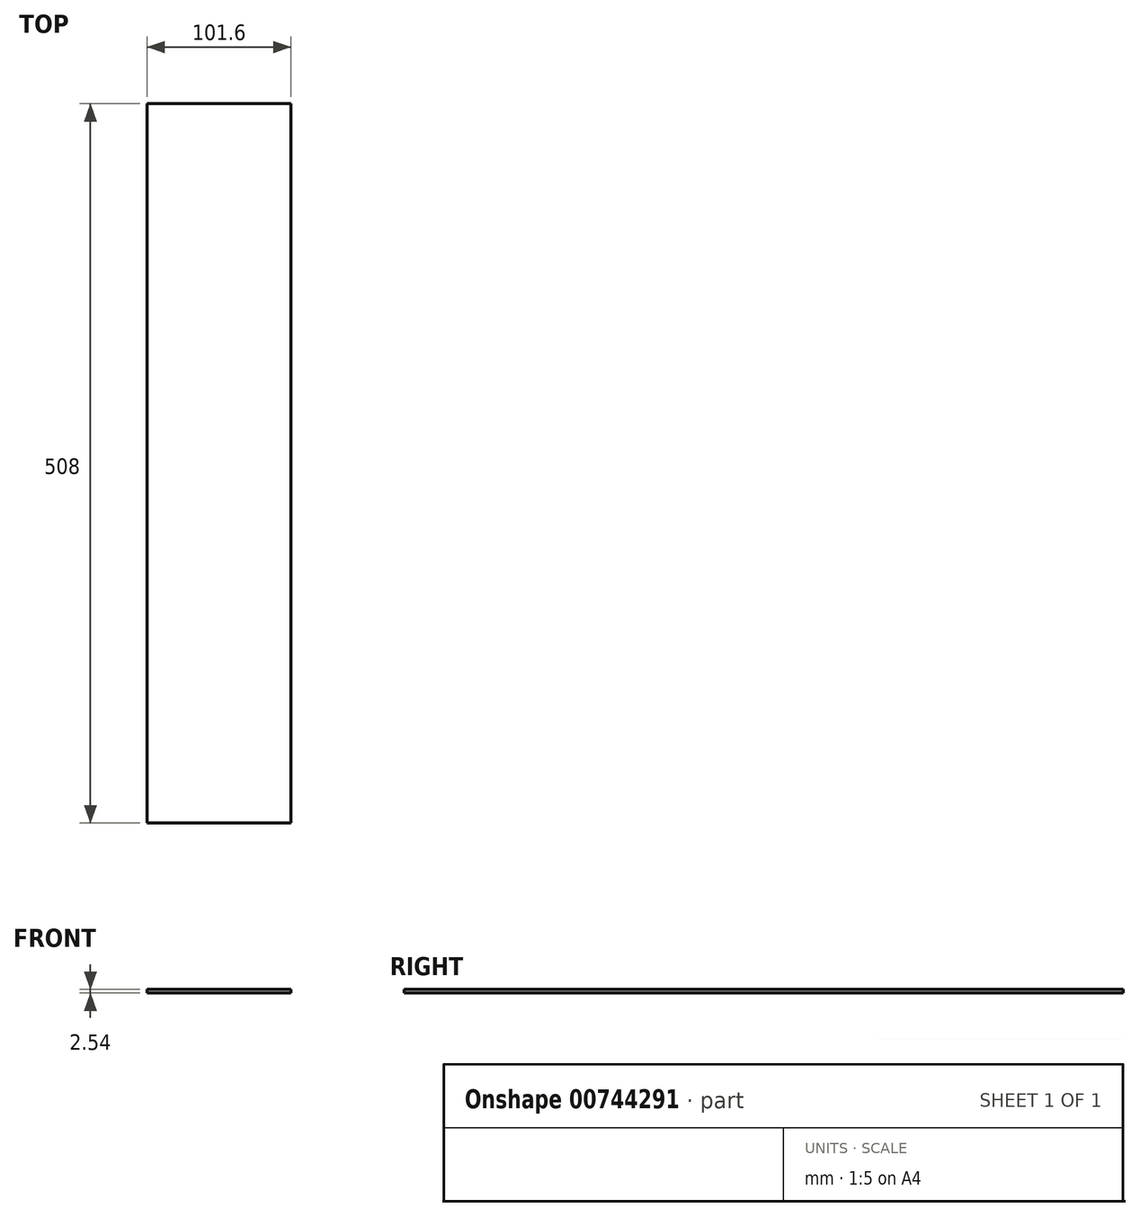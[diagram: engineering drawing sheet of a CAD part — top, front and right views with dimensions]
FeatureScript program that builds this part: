
annotation { "Feature Type Name" : "Feature", "Feature Type Description" : "" }
export const myFeature = defineFeature(function(context is Context, id is Id, definition is map)
    precondition{}
    {
        {
            var Q0;
            Q0=qCreatedBy(makeId("Top.planeOp"),FACE);
            var sketch = newSketch(context, id + "F0", { "sketchPlane" : qUnion([Q0])});
            skLineSegment(sketch, "E0.bottom", {"start": v(-50.8, -254) * mm, "end": v(50.8, -254) * mm});
            skLineSegment(sketch, "E0.top", {"start": v(-50.8, 254) * mm, "end": v(50.8, 254) * mm});
            skLineSegment(sketch, "E0.left", {"start": v(-50.8, -254) * mm, "end": v(-50.8, 254) * mm});
            skLineSegment(sketch, "E0.right", {"start": v(50.8, -254) * mm, "end": v(50.8, 254) * mm});
            skSolve(sketch);
        }
        {
            var Q0;
            Q0=sQuery(id+"F0.wireOp",EDGE,"E0.right");
            var Q1;
            Q1=sQuery(id+"F0.wireOp",EDGE,"E0.top");
            var Q2;
            Q2=sQuery(id+"F0.wireOp",EDGE,"E0.left");
            var Q3;
            Q3=sQuery(id+"F0.wireOp",EDGE,"E0.bottom");
            extrude(context, id + "F1", {"bodyType" : ToolBodyType.SURFACE, "surfaceEntities" : qUnion([Q0, Q1, Q2, Q3]), "depth" : 6.35 * mm, "offsetDistance" : 25.4 * mm});
        }
        {
            var Q0;
            Q0=makeQuery(id+"F0.imprint","IMPRINT",FACE,{"disambiguationData":[TD([[makeQuery(id+"F0.imprint","IMPRINT",EDGE,{"derivedFrom":sQuery(id+"F0.wireOp",EDGE,"E0.bottom")}),1.0]])]});
            extrude(context, id + "F2", {"entities" : qUnion([Q0]), "depth" : 2.54 * mm, "offsetDistance" : 25.4 * mm});
        }
    });
